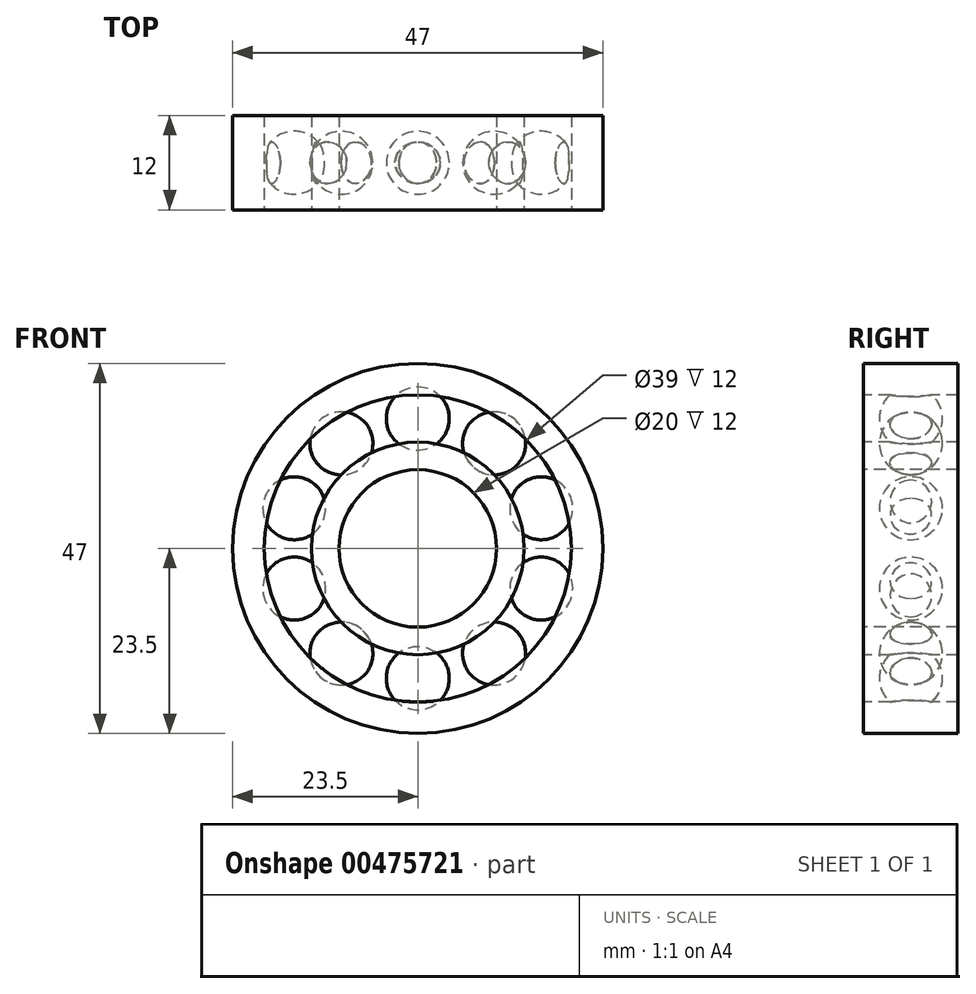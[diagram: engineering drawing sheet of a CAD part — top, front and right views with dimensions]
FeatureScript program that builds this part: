
annotation { "Feature Type Name" : "Feature", "Feature Type Description" : "" }
export const myFeature = defineFeature(function(context is Context, id is Id, definition is map)
    precondition{}
    {
        {
            var Q0;
            Q0=qCreatedBy(makeId("Front.planeOp"),FACE);
            var sketch = newSketch(context, id + "F0", { "sketchPlane" : qUnion([Q0])});
            skCircle(sketch, "E0", {"center": v(0, 0) * mm, "radius": 10 * mm});
            skCircle(sketch, "E1", {"center": v(0, 0) * mm, "radius": 13.5 * mm});
            skSolve(sketch);
        }
        {
            var Q0;
            Q0=qCreatedBy(makeId("Front.planeOp"),FACE);
            var sketch = newSketch(context, id + "F1", { "sketchPlane" : qUnion([Q0])});
            skCircle(sketch, "E2", {"center": v(0, 0) * mm, "radius": 19.5 * mm});
            skCircle(sketch, "E3", {"center": v(0, 0) * mm, "radius": 23.5 * mm});
            skSolve(sketch);
        }
        {
            var Q0;
            Q0=makeQuery(id+"F1.imprint","IMPRINT",FACE,{"disambiguationData":[TD([[makeQuery(id+"F1.imprint","IMPRINT",EDGE,{"derivedFrom":sQuery(id+"F1.wireOp",EDGE,"E2")}),-1.0]])]});
            extrude(context, id + "F2", {"entities" : qUnion([Q0]), "oppositeDirection" : true, "depth" : 12 * mm});
        }
        {
            var Q0;
            Q0 = qSketchRegion(id + "F0", true);
            extrude(context, id + "F3", {"entities" : qUnion([Q0]), "oppositeDirection" : true, "depth" : 12 * mm});
        }
        {
            var Q0;
            Q0=qCreatedBy(makeId("Front.planeOp"),FACE);
            cPlane(context, id + "F4", {"entities" : qUnion([Q0]), "cplaneType" : CPlaneType.OFFSET, "offset" : 6 * mm, "oppositeDirection" : true, "width" : 150 * mm, "height" : 150 * mm});
        }
        {
            var Q0;
            Q0=qCreatedBy(id+"F4.planeOp",FACE);
            var sketch = newSketch(context, id + "F5", { "sketchPlane" : qUnion([Q0])});
            skArc(sketch, "E4", {"start": v(0, 12.5) * mm, "mid": v(4, 16.5) * mm, "end": v(0, 20.5) * mm});
            skLineSegment(sketch, "E5", {"start": v(0, 12.5) * mm, "end": v(0, 20.5) * mm});
            skSolve(sketch);
        }
        {
            var Q0;
            Q0 = qSketchRegion(id + "F5", true);
            var Q1;
            Q1=sQuery(id+"F5.wireOp",EDGE,"E5");
            revolve(context, id + "F6", {"entities" : qUnion([Q0]), "axis" : qUnion([Q1]), "revolveType" : RevolveType.FULL});
        }
        {
            var Q0;
            Q0=qCreatedBy(makeId("Right.planeOp"),FACE);
            var sketch = newSketch(context, id + "F7", { "sketchPlane" : qUnion([Q0])});
            skLineSegment(sketch, "E6", {"start": v(-46.3, 0) * mm, "end": v(43.84, 0) * mm, "construction": true});
            skSolve(sketch);
        }
        {
            var Q0;
            Q0=makeQuery(id+"F6.opRevolve","SWEPT_BODY",BODY,{"disambiguationData":[OSD([sQuery(id+"F5.wireOp",EDGE,"E4"),sQuery(id+"F5.wireOp",EDGE,"E5")])]});
            var Q1;
            Q1=sQuery(id+"F7.wireOp",EDGE,"E6");
            circularPattern(context, id + "F8", {"operationType" : NewBodyOperationType.ADD, "entities" : qUnion([Q0]), "axis" : qUnion([Q1]), "angle" : 360 * degree, "instanceCount" : 10, "equalSpace" : true});
        }
    });
